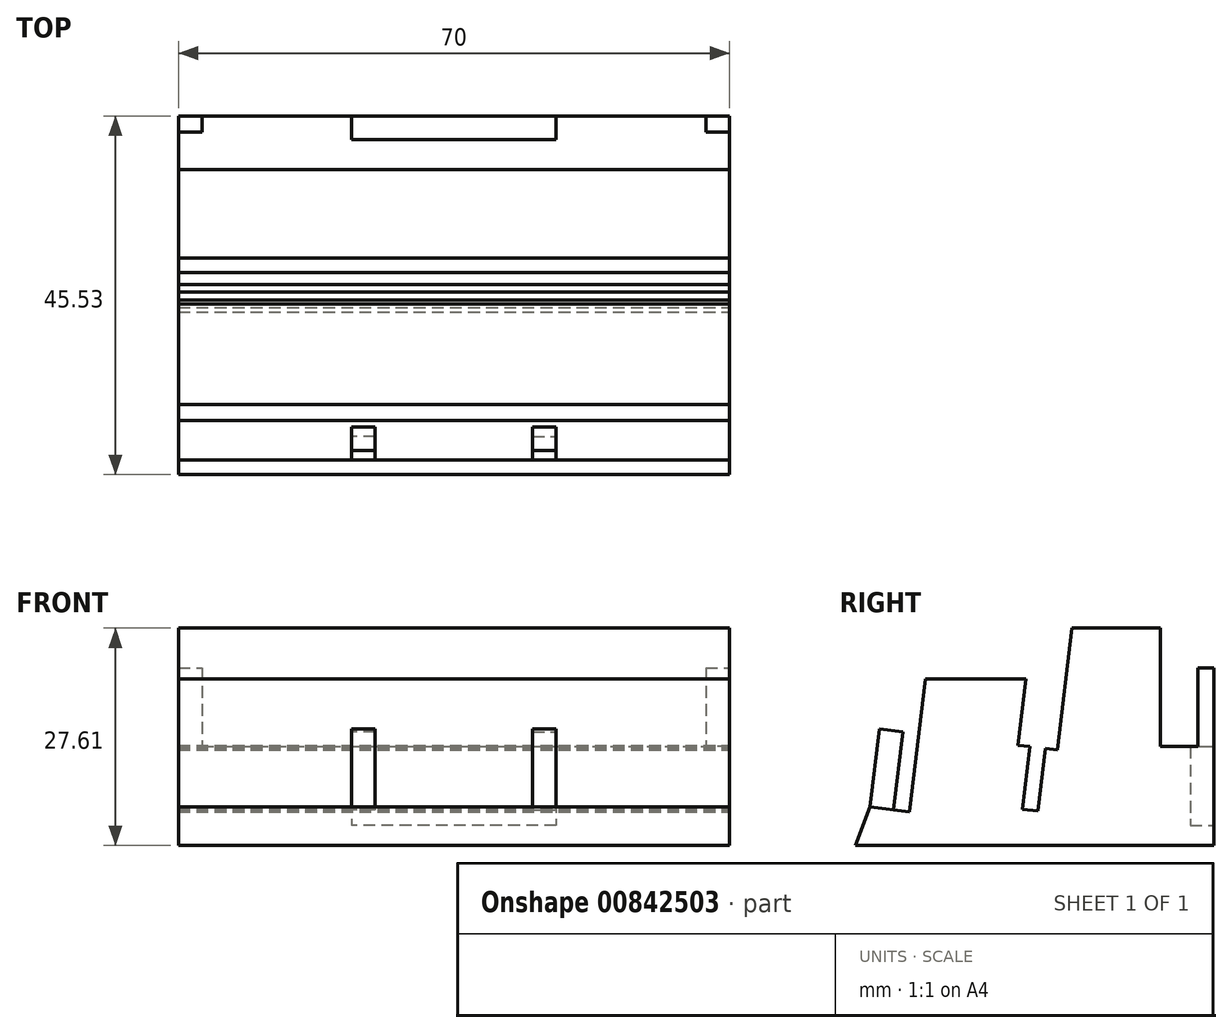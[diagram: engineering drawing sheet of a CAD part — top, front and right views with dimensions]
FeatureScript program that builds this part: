
annotation { "Feature Type Name" : "Feature", "Feature Type Description" : "" }
export const myFeature = defineFeature(function(context is Context, id is Id, definition is map)
    precondition{}
    {
        {
            var Q0;
            Q0=qCreatedBy(makeId("Right.planeOp"),FACE);
            var sketch = newSketch(context, id + "F0", { "sketchPlane" : qUnion([Q0])});
            skLineSegment(sketch, "E0", {"start": v(0, 0) * mm, "end": v(-20.48, 0) * mm});
            skLineSegment(sketch, "E1", {"start": v(-20.48, 0) * mm, "end": v(-9.84, 27.61) * mm});
            skLineSegment(sketch, "E2", {"start": v(25.05, 27.61) * mm, "end": v(25.05, 0) * mm});
            skLineSegment(sketch, "E3", {"start": v(25.05, 0) * mm, "end": v(0, 0) * mm});
            skLineSegment(sketch, "E4", {"start": v(-9.84, 27.61) * mm, "end": v(25.05, 27.61) * mm});
            skSolve(sketch);
        }
        {
            var Q0;
            Q0=makeQuery(id+"F0.imprint","IMPRINT",FACE,{"disambiguationData":[TD([[makeQuery(id+"F0.imprint","IMPRINT",EDGE,{"derivedFrom":sQuery(id+"F0.wireOp",EDGE,"E0")}),-1.0]])]});
            extrude(context, id + "F1", {"entities" : qUnion([Q0]), "endBound" : BoundingType.SYMMETRIC, "depth" : 70 * mm, "offsetDistance" : 25 * mm});
        }
        {
            var Q0;
            Q0=makeQuery(id+"F1.opExtrude","CAP_FACE",FACE,{"disambiguationData":[OSD([sQuery(id+"F0.wireOp",EDGE,"E0"),sQuery(id+"F0.wireOp",EDGE,"E1"),sQuery(id+"F0.wireOp",EDGE,"E2"),sQuery(id+"F0.wireOp",EDGE,"E3"),sQuery(id+"F0.wireOp",EDGE,"E4")])],"isStart":false});
            var sketch = newSketch(context, id + "F2", { "sketchPlane" : qUnion([Q0])});
            skLineSegment(sketch, "E5", {"start": v(2, 27.61) * mm, "end": v(0.19, 12.72) * mm});
            skLineSegment(sketch, "E6", {"start": v(5.15, 12.12) * mm, "end": v(7.03, 27.61) * mm});
            skLineSegment(sketch, "E7", {"start": v(1.68, 12.54) * mm, "end": v(0.71, 4.6) * mm});
            skLineSegment(sketch, "E8", {"start": v(0.71, 4.6) * mm, "end": v(2.7, 4.36) * mm});
            skLineSegment(sketch, "E9", {"start": v(2.7, 4.36) * mm, "end": v(3.66, 12.3) * mm});
            skLineSegment(sketch, "E10", {"start": v(0.19, 12.72) * mm, "end": v(1.68, 12.54) * mm});
            skLineSegment(sketch, "E11", {"start": v(3.66, 12.3) * mm, "end": v(5.15, 12.12) * mm});
            skLineSegment(sketch, "E12", {"start": v(-10.81, 27.61) * mm, "end": v(-13.64, 4.26) * mm});
            skLineSegment(sketch, "E13", {"start": v(-13.64, 4.26) * mm, "end": v(-18.6, 4.86) * mm});
            skLineSegment(sketch, "E14", {"start": v(18.24, 27.61) * mm, "end": v(18.24, 12.55) * mm});
            skLineSegment(sketch, "E15", {"start": v(18.24, 12.55) * mm, "end": v(25.05, 12.55) * mm});
            skSolve(sketch);
        }
        {
            var Q0;
            {var subQ1=sQuery(id+"F2.wireOp",EDGE,"E5");Q0=makeQuery(id+"F2.imprint","IMPRINT",FACE,{"disambiguationData":[TD([[makeQuery(id+"F2.imprint","IMPRINT",EDGE,{"derivedFrom":subQ1}),1.0]])]});}
            var Q1;
            Q1=makeQuery(id+"F2.imprint","IMPRINT",FACE,{"disambiguationData":[TD([[makeQuery(id+"F2.imprint","IMPRINT",EDGE,{"derivedFrom":sQuery(id+"F2.wireOp",EDGE,"E12")}),-1.0]])]});
            var Q2;
            {var subQ0=sQuery(id+"F2.wireOp",EDGE,"E14");Q2=makeQuery(id+"F2.imprint","IMPRINT",FACE,{"disambiguationData":[TD([[makeQuery(id+"F2.imprint","IMPRINT",EDGE,{"derivedFrom":subQ0}),1.0]])]});}
            var Q3;
            Q3=makeQuery(id+"F1.opExtrude","SWEPT_BODY",BODY,{"disambiguationData":[OSD([sQuery(id+"F0.wireOp",EDGE,"E0"),sQuery(id+"F0.wireOp",EDGE,"E1"),sQuery(id+"F0.wireOp",EDGE,"E2"),sQuery(id+"F0.wireOp",EDGE,"E3"),sQuery(id+"F0.wireOp",EDGE,"E4")])]});
            extrude(context, id + "F3", {"entities" : qUnion([Q0, Q1, Q2]), "operationType" : NewBodyOperationType.REMOVE, "endBound" : BoundingType.UP_TO_BODY, "oppositeDirection" : true, "depth" : 25 * mm, "endBoundEntityBody" : qUnion([Q3]), "offsetDistance" : 25 * mm});
        }
        {
            var Q0;
            Q0=makeQuery(id+"F1.opExtrude","CAP_FACE",FACE,{"disambiguationData":[OSD([sQuery(id+"F0.wireOp",EDGE,"E0"),sQuery(id+"F0.wireOp",EDGE,"E1"),sQuery(id+"F0.wireOp",EDGE,"E2"),sQuery(id+"F0.wireOp",EDGE,"E3"),sQuery(id+"F0.wireOp",EDGE,"E4")])],"isStart":false});
            var sketch = newSketch(context, id + "F4", { "sketchPlane" : qUnion([Q0])});
            skLineSegment(sketch, "E16", {"start": v(-12.33, 21.16) * mm, "end": v(1.2, 21.16) * mm});
            skLineSegment(sketch, "E17", {"start": v(1.2, 21.16) * mm, "end": v(2, 27.61) * mm});
            skSolve(sketch);
        }
        {
            var Q0;
            {var subQ0=sQuery(id+"F4.wireOp",EDGE,"E16");Q0=makeQuery(id+"F4.imprint","IMPRINT",FACE,{"disambiguationData":[TD([[makeQuery(id+"F4.imprint","IMPRINT",EDGE,{"derivedFrom":subQ0}),1.0]])]});}
            var Q1;
            Q1=makeQuery(id+"F1.opExtrude","SWEPT_BODY",BODY,{"disambiguationData":[OSD([sQuery(id+"F0.wireOp",EDGE,"E0"),sQuery(id+"F0.wireOp",EDGE,"E1"),sQuery(id+"F0.wireOp",EDGE,"E2"),sQuery(id+"F0.wireOp",EDGE,"E3"),sQuery(id+"F0.wireOp",EDGE,"E4")])]});
            extrude(context, id + "F5", {"entities" : qUnion([Q0]), "operationType" : NewBodyOperationType.REMOVE, "endBound" : BoundingType.UP_TO_BODY, "oppositeDirection" : true, "depth" : 25 * mm, "endBoundEntityBody" : qUnion([Q1]), "offsetDistance" : 25 * mm});
        }
        {
            var Q0;
            Q0=makeQuery(id+"F3.boolean.opBoolean","COPY",FACE,{"derivedFrom":makeQuery(id+"F3.opExtrude","SWEPT_FACE",FACE,{"disambiguationData":[OSD([sQuery(id+"F2.wireOp",EDGE,"E13")])]})});
            var sketch = newSketch(context, id + "F6", { "sketchPlane" : qUnion([Q0])});
            skLineSegment(sketch, "E18", {"start": v(0, -19.06) * mm, "end": v(-10, -19.06) * mm});
            skLineSegment(sketch, "E19", {"start": v(-10, -19.06) * mm, "end": v(-10, -16.06) * mm});
            skLineSegment(sketch, "E20", {"start": v(-10, -16.06) * mm, "end": v(-13, -16.06) * mm});
            skLineSegment(sketch, "E21", {"start": v(-13, -16.06) * mm, "end": v(-13, -19.06) * mm});
            skLineSegment(sketch, "E22.MirrorCS", {"start": v(13, -16.06) * mm, "end": v(13, -19.06) * mm});
            skLineSegment(sketch, "E23.MirrorCS", {"start": v(10, -16.06) * mm, "end": v(13, -16.06) * mm});
            skLineSegment(sketch, "E24.MirrorCS", {"start": v(10, -19.06) * mm, "end": v(10, -16.06) * mm});
            skSolve(sketch);
        }
        {
            var Q0;
            {var subQ0=sQuery(id+"F6.wireOp",EDGE,"E22.MirrorCS");Q0=makeQuery(id+"F6.imprint","IMPRINT",FACE,{"disambiguationData":[TD([[makeQuery(id+"F6.imprint","IMPRINT",EDGE,{"derivedFrom":subQ0}),-1.0]])]});}
            var Q1;
            {var subQ0=sQuery(id+"F6.wireOp",EDGE,"E19");Q1=makeQuery(id+"F6.imprint","IMPRINT",FACE,{"disambiguationData":[TD([[makeQuery(id+"F6.imprint","IMPRINT",EDGE,{"derivedFrom":subQ0}),1.0]])]});}
            extrude(context, id + "F7", {"entities" : qUnion([Q0, Q1]), "operationType" : NewBodyOperationType.ADD, "depth" : 10 * mm, "offsetDistance" : 25 * mm});
        }
        {
            var Q0;
            Q0=makeQuery(id+"F3.boolean.opBoolean","COPY",FACE,{"derivedFrom":makeQuery(id+"F3.opExtrude","SWEPT_FACE",FACE,{"disambiguationData":[OSD([sQuery(id+"F2.wireOp",EDGE,"E15")])]})});
            var sketch = newSketch(context, id + "F8", { "sketchPlane" : qUnion([Q0])});
            skLineSegment(sketch, "E25", {"start": v(0, 25.05) * mm, "end": v(32, 25.05) * mm});
            skLineSegment(sketch, "E26", {"start": v(35, 25.05) * mm, "end": v(35, 23.05) * mm});
            skLineSegment(sketch, "E27", {"start": v(35, 23.05) * mm, "end": v(32, 23.05) * mm});
            skLineSegment(sketch, "E28", {"start": v(32, 23.05) * mm, "end": v(32, 25.05) * mm});
            skLineSegment(sketch, "E29.MirrorCS", {"start": v(-32, 23.05) * mm, "end": v(-32, 25.05) * mm});
            skLineSegment(sketch, "E30.MirrorCS", {"start": v(-35, 23.05) * mm, "end": v(-32, 23.05) * mm});
            skLineSegment(sketch, "E31.MirrorCS", {"start": v(-35, 25.05) * mm, "end": v(-35, 23.05) * mm});
            skSolve(sketch);
        }
        {
            var Q0;
            {var subQ0=sQuery(id+"F8.wireOp",EDGE,"E26");Q0=makeQuery(id+"F8.imprint","IMPRINT",FACE,{"disambiguationData":[TD([[makeQuery(id+"F8.imprint","IMPRINT",EDGE,{"derivedFrom":subQ0}),1.0]])]});}
            var Q1;
            {var subQ0=sQuery(id+"F8.wireOp",EDGE,"E29.MirrorCS");Q1=makeQuery(id+"F8.imprint","IMPRINT",FACE,{"disambiguationData":[TD([[makeQuery(id+"F8.imprint","IMPRINT",EDGE,{"derivedFrom":subQ0}),1.0]])]});}
            extrude(context, id + "F9", {"entities" : qUnion([Q0, Q1]), "operationType" : NewBodyOperationType.ADD, "depth" : 10 * mm, "offsetDistance" : 25 * mm});
        }
        {
            var Q0;
            Q0=makeQuery(id+"F1.opExtrude","SWEPT_FACE",FACE,{"disambiguationData":[OSD([sQuery(id+"F0.wireOp",EDGE,"E2")])]});
            var sketch = newSketch(context, id + "F10", { "sketchPlane" : qUnion([Q0])});
            skLineSegment(sketch, "E32", {"start": v(0, 12.55) * mm, "end": v(-13, 12.55) * mm});
            skLineSegment(sketch, "E33.bottom", {"start": v(-13, 12.55) * mm, "end": v(13, 12.55) * mm});
            skLineSegment(sketch, "E33.top", {"start": v(-13, 2.55) * mm, "end": v(13, 2.55) * mm});
            skLineSegment(sketch, "E33.left", {"start": v(-13, 12.55) * mm, "end": v(-13, 2.55) * mm});
            skLineSegment(sketch, "E33.right", {"start": v(13, 12.55) * mm, "end": v(13, 2.55) * mm});
            skSolve(sketch);
        }
        {
            var Q0;
            Q0=makeQuery(id+"F10.imprint","IMPRINT",FACE,{"disambiguationData":[TD([[makeQuery(id+"F10.imprint","IMPRINT",EDGE,{"derivedFrom":sQuery(id+"F10.wireOp",EDGE,"E33.top")}),1.0]])]});
            extrude(context, id + "F11", {"entities" : qUnion([Q0]), "operationType" : NewBodyOperationType.REMOVE, "oppositeDirection" : true, "depth" : 3 * mm, "offsetDistance" : 25 * mm});
        }
    });
